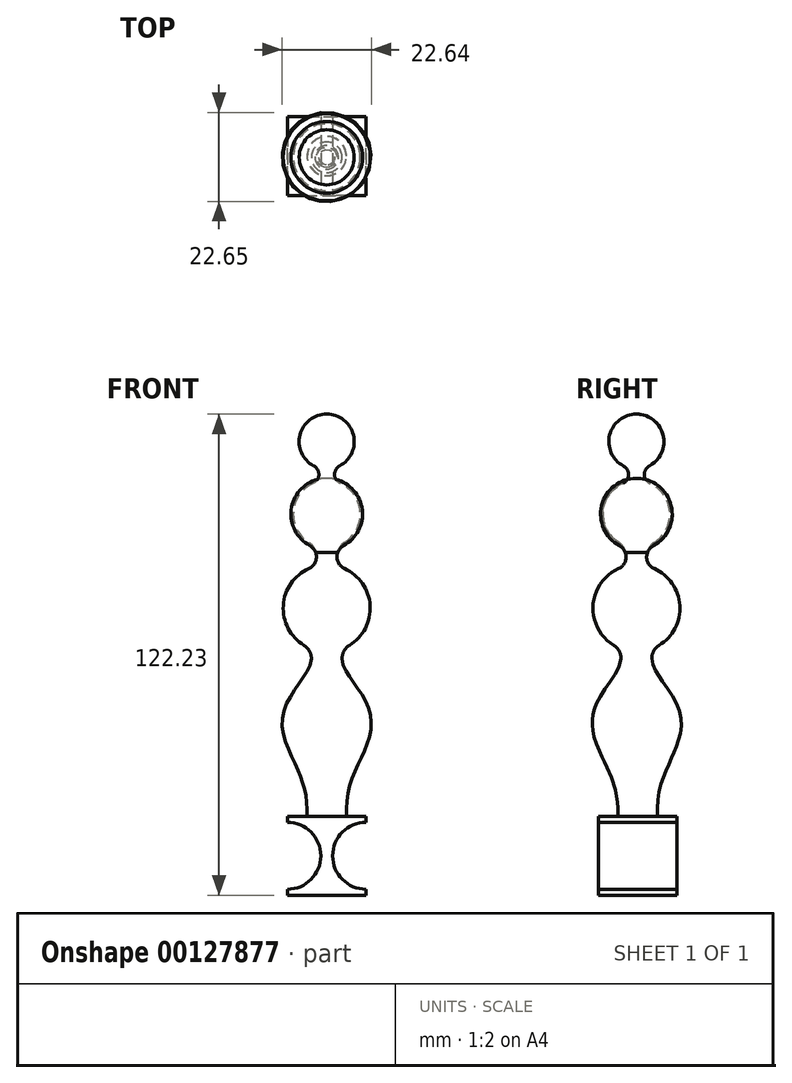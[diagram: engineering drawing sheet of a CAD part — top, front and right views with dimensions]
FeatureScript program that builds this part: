
annotation { "Feature Type Name" : "Feature", "Feature Type Description" : "" }
export const myFeature = defineFeature(function(context is Context, id is Id, definition is map)
    precondition{}
    {
        {
            var Q0;
            Q0=qCreatedBy(makeId("Top.planeOp"),FACE);
            var sketch = newSketch(context, id + "F0", { "sketchPlane" : qUnion([Q0])});
            skLineSegment(sketch, "E0.bottom", {"start": v(-10, -10) * mm, "end": v(10, -10) * mm});
            skLineSegment(sketch, "E0.top", {"start": v(-10, 10) * mm, "end": v(10, 10) * mm});
            skLineSegment(sketch, "E0.left", {"start": v(-10, -10) * mm, "end": v(-10, 10) * mm});
            skLineSegment(sketch, "E0.right", {"start": v(10, -10) * mm, "end": v(10, 10) * mm});
            skPoint(sketch, "E0.middle", {"position": v(0, 0) * mm});
            skSolve(sketch);
        }
        {
            var Q0;
            Q0=makeQuery(id+"F0.imprint","IMPRINT",FACE,{"disambiguationData":[TD([[makeQuery(id+"F0.imprint","IMPRINT",EDGE,{"derivedFrom":sQuery(id+"F0.wireOp",EDGE,"E0.bottom")}),1.0]])]});
            extrude(context, id + "F1", {"entities" : qUnion([Q0]), "depth" : 20 * mm});
        }
        {
            var Q0;
            Q0=makeQuery(id+"F1.opExtrude","SWEPT_FACE",FACE,{"disambiguationData":[OSD([sQuery(id+"F0.wireOp",EDGE,"E0.bottom")])]});
            var sketch = newSketch(context, id + "F2", { "sketchPlane" : qUnion([Q0])});
            skCircle(sketch, "E1", {"center": v(-10, 10) * mm, "radius": 8.5 * mm});
            skCircle(sketch, "E2", {"center": v(10, 10) * mm, "radius": 8.5 * mm});
            skSolve(sketch);
        }
        {
            var Q0;
            {var subQ0=sQuery(id+"F2.wireOp",EDGE,"E2");var subQ1=makeQuery(id+"F1.opExtrude","SWEPT_EDGE",EDGE,{"disambiguationData":[OSD([sQuery(id+"F0.wireOp",EDGE,"E0.bottom"),sQuery(id+"F0.wireOp",EDGE,"E0.right")])]});var subQ2=makeQuery(id+"F2.imprint","INTERSECT",VERTEX,{"disambiguationData":[OD(0.0)],"derivedFrom":[subQ1,subQ0]});Q0=makeQuery(id+"F2.imprint","IMPRINT",FACE,{"disambiguationData":[TD([[makeQuery(id+"F2.imprint","IMPRINT",EDGE,{"disambiguationData":[TD([[subQ2,1.0]])],"derivedFrom":subQ0}),1.0]])]});}
            var Q1;
            {var subQ0=sQuery(id+"F2.wireOp",EDGE,"E1");var subQ1=makeQuery(id+"F1.opExtrude","SWEPT_EDGE",EDGE,{"disambiguationData":[OSD([sQuery(id+"F0.wireOp",EDGE,"E0.bottom"),sQuery(id+"F0.wireOp",EDGE,"E0.left")])]});var subQ2=makeQuery(id+"F2.imprint","INTERSECT",VERTEX,{"disambiguationData":[OD(0.0)],"derivedFrom":[subQ1,subQ0]});Q1=makeQuery(id+"F2.imprint","IMPRINT",FACE,{"disambiguationData":[TD([[makeQuery(id+"F2.imprint","IMPRINT",EDGE,{"disambiguationData":[TD([[subQ2,-1.0]])],"derivedFrom":subQ0}),1.0]])]});}
            extrude(context, id + "F3", {"entities" : qUnion([Q0, Q1]), "operationType" : NewBodyOperationType.REMOVE, "endBound" : BoundingType.THROUGH_ALL, "oppositeDirection" : true, "depth" : 25 * mm});
        }
        {
            var Q0;
            Q0=qCreatedBy(makeId("Right.planeOp"),FACE);
            var sketch = newSketch(context, id + "F4", { "sketchPlane" : qUnion([Q0])});
            skLineSegment(sketch, "E3.0", {"start": v(-10, 20) * mm, "end": v(10, 20) * mm, "construction": true});
            skArc(sketch, "E4", {"start": v(0, 20) * mm, "mid": v(2.28, 37.3) * mm, "end": v(8.96, 53.42) * mm});
            skLineSegment(sketch, "E5", {"start": v(0, 20) * mm, "end": v(66.85, 20) * mm, "construction": true});
            skLineSegment(sketch, "E6", {"start": v(66.85, 20) * mm, "end": v(8.96, 53.42) * mm, "construction": true});
            skCircle(sketch, "E7", {"center": v(8.96, 53.42) * mm, "radius": 8.5 * mm});
            skLineSegment(sketch, "E8", {"start": v(8.96, 53.42) * mm, "end": v(27.36, 85.3) * mm, "construction": true});
            skCircle(sketch, "E9", {"center": v(18.16, 69.36) * mm, "radius": 7 * mm});
            skCircle(sketch, "E10", {"center": v(10.08, 64.37) * mm, "radius": 2.5 * mm});
            skPoint(sketch, "E11", {"position": v(1.49, 49.36) * mm});
            skPoint(sketch, "E12", {"position": v(13.2, 60.78) * mm});
            skPoint(sketch, "E13", {"position": v(12.2, 65.68) * mm});
            skPoint(sketch, "E14", {"position": v(9.82, 61.88) * mm});
            skPoint(sketch, "E15", {"position": v(21.66, 75.42) * mm});
            skLineSegment(sketch, "E16", {"start": v(21.66, 75.42) * mm, "end": v(0, 37.91) * mm});
            skCircle(sketch, "E17", {"center": v(-1.15, 47.93) * mm, "radius": 3 * mm});
            skLineSegment(sketch, "E18", {"start": v(4.05, 44.93) * mm, "end": v(1.45, 46.43) * mm});
            skLineSegment(sketch, "E19", {"start": v(1.45, 46.43) * mm, "end": v(-2.2, 48.54) * mm, "construction": true});
            skArc(sketch, "E20", {"start": v(0, 20) * mm, "mid": v(1.02, 32.63) * mm, "end": v(4.05, 44.93) * mm});
            skSolve(sketch);
        }
        {
            var Q0;
            {var subQ5=sQuery(id+"F4.wireOp",EDGE,"E18");Q0=makeQuery(id+"F4.imprint","IMPRINT",FACE,{"disambiguationData":[TD([[makeQuery(id+"F4.imprint","IMPRINT",EDGE,{"derivedFrom":subQ5}),-1.0]])]});}
            var Q1;
            {var subQ2=sQuery(id+"F4.wireOp",EDGE,"E7");var subQ4=makeQuery(id+"F4.imprint","INTERSECT",VERTEX,{"derivedFrom":[subQ2,sQuery(id+"F4.wireOp",EDGE,"E10")]});Q1=makeQuery(id+"F4.imprint","IMPRINT",FACE,{"disambiguationData":[TD([[makeQuery(id+"F4.imprint","IMPRINT",EDGE,{"disambiguationData":[TD([[subQ4,1.0]])],"derivedFrom":subQ2}),1.0]])]});}
            var Q2;
            {var subQ0=sQuery(id+"F4.wireOp",EDGE,"E10");var subQ1=sQuery(id+"F4.wireOp",EDGE,"E7");var subQ2=makeQuery(id+"F4.imprint","INTERSECT",VERTEX,{"derivedFrom":[subQ1,subQ0]});Q2=makeQuery(id+"F4.imprint","IMPRINT",FACE,{"disambiguationData":[TD([[makeQuery(id+"F4.imprint","IMPRINT",EDGE,{"disambiguationData":[TD([[subQ2,1.0]])],"derivedFrom":subQ1}),-1.0]])]});}
            var Q3;
            {var subQ0=sQuery(id+"F4.wireOp",EDGE,"E16");var subQ1=sQuery(id+"F4.wireOp",EDGE,"E9");var subQ2=makeQuery(id+"F4.imprint","INTERSECT",VERTEX,{"disambiguationData":[OD(0.0)],"derivedFrom":[subQ1,subQ0]});Q3=makeQuery(id+"F4.imprint","IMPRINT",FACE,{"disambiguationData":[TD([[makeQuery(id+"F4.imprint","IMPRINT",EDGE,{"disambiguationData":[TD([[subQ2,-1.0]])],"derivedFrom":subQ1}),1.0]])]});}
            var Q4;
            Q4=sQuery(id+"F4.wireOp",EDGE,"E16");
            revolve(context, id + "F5", {"entities" : qUnion([Q0, Q1, Q2, Q3]), "axis" : qUnion([Q4]), "revolveType" : RevolveType.FULL});
        }
        {
            var Q0;
            Q0=makeQuery(id+"F1.opExtrude","CAP_FACE",FACE,{"disambiguationData":[OSD([sQuery(id+"F0.wireOp",EDGE,"E0.bottom"),sQuery(id+"F0.wireOp",EDGE,"E0.top"),sQuery(id+"F0.wireOp",EDGE,"E0.left"),sQuery(id+"F0.wireOp",EDGE,"E0.right")])],"isStart":false});
            var sketch = newSketch(context, id + "F6", { "sketchPlane" : qUnion([Q0])});
            skCircle(sketch, "E21", {"center": v(0, 0) * mm, "radius": 5 * mm});
            skSolve(sketch);
        }
        {
            var Q0;
            Q0=qCreatedBy(makeId("Right.planeOp"),FACE);
            var sketch = newSketch(context, id + "F7", { "sketchPlane" : qUnion([Q0])});
            skPoint(sketch, "E22.0", {"position": v(8.96, 53.42) * mm});
            skPoint(sketch, "E23.0", {"position": v(18.16, 69.36) * mm});
            skLineSegment(sketch, "E24", {"start": v(8.96, 53.42) * mm, "end": v(18.16, 69.36) * mm, "construction": true});
            skSolve(sketch);
        }
        {
            var Q0;
            Q0=makeQuery(id+"F5.opRevolve","SWEPT_BODY",BODY,{"disambiguationData":[OSD([sQuery(id+"F4.wireOp",EDGE,"E7"),sQuery(id+"F4.wireOp",EDGE,"E9"),sQuery(id+"F4.wireOp",EDGE,"E10"),sQuery(id+"F4.wireOp",EDGE,"E16"),sQuery(id+"F4.wireOp",EDGE,"E17"),sQuery(id+"F4.wireOp",EDGE,"E18")])]});
            var Q1;
            Q1=sQuery(id+"F7.wireOp",EDGE,"E24");
            transform(context, id + "F8", {"entities" : qUnion([Q0]), "transformType" : TransformType.TRANSLATION_ENTITY, "oppositeDirectionEntity" : false, "transformLine" : qUnion([Q1]), "makeCopy" : true});
        }
        {
            var Q0;
            Q0=makeQuery(id+"F5.opRevolve","SWEPT_BODY",BODY,{"disambiguationData":[OSD([sQuery(id+"F4.wireOp",EDGE,"E7"),sQuery(id+"F4.wireOp",EDGE,"E9"),sQuery(id+"F4.wireOp",EDGE,"E10"),sQuery(id+"F4.wireOp",EDGE,"E16"),sQuery(id+"F4.wireOp",EDGE,"E17"),sQuery(id+"F4.wireOp",EDGE,"E18")])]});
            var Q1;
            Q1=sQuery(id+"F7.wireOp",VERTEX,"E23.0");
            transform(context, id + "F9", {"entities" : qUnion([Q0]), "transformType" : TransformType.SCALE_UNIFORMLY, "scale" : 1.3, "scalePoint" : qUnion([Q1]), "makeCopy" : false});
        }
        {
            var Q0;
            Q0=makeQuery(id+"F5.opRevolve","SWEPT_BODY",BODY,{"disambiguationData":[OSD([sQuery(id+"F4.wireOp",EDGE,"E7"),sQuery(id+"F4.wireOp",EDGE,"E9"),sQuery(id+"F4.wireOp",EDGE,"E10"),sQuery(id+"F4.wireOp",EDGE,"E16"),sQuery(id+"F4.wireOp",EDGE,"E17"),sQuery(id+"F4.wireOp",EDGE,"E18")])]});
            var Q1;
            Q1=makeQuery(id+"F8.opPattern","COPY",BODY,{"derivedFrom":makeQuery(id+"F5.opRevolve","SWEPT_BODY",BODY,{"disambiguationData":[OSD([sQuery(id+"F4.wireOp",EDGE,"E7"),sQuery(id+"F4.wireOp",EDGE,"E9"),sQuery(id+"F4.wireOp",EDGE,"E10"),sQuery(id+"F4.wireOp",EDGE,"E16"),sQuery(id+"F4.wireOp",EDGE,"E17"),sQuery(id+"F4.wireOp",EDGE,"E18")])]}),"instanceName":"1"});
            var Q2;
            Q2=makeQuery(id+"F1.opExtrude","CAP_EDGE",EDGE,{"disambiguationData":[OSD([sQuery(id+"F0.wireOp",EDGE,"E0.bottom")])],"isStart":false});
            transform(context, id + "F10", {"entities" : qUnion([Q0, Q1]), "transformType" : TransformType.ROTATION, "transformAxis" : qUnion([Q2]), "angle" : 30 * degree, "makeCopy" : false});
        }
        {
            var Q0;
            Q0=makeQuery(id+"F5.opRevolve","SWEPT_BODY",BODY,{"disambiguationData":[OSD([sQuery(id+"F4.wireOp",EDGE,"E7"),sQuery(id+"F4.wireOp",EDGE,"E9"),sQuery(id+"F4.wireOp",EDGE,"E10"),sQuery(id+"F4.wireOp",EDGE,"E16"),sQuery(id+"F4.wireOp",EDGE,"E17"),sQuery(id+"F4.wireOp",EDGE,"E18")])]});
            var Q1;
            Q1=makeQuery(id+"F8.opPattern","COPY",BODY,{"derivedFrom":makeQuery(id+"F5.opRevolve","SWEPT_BODY",BODY,{"disambiguationData":[OSD([sQuery(id+"F4.wireOp",EDGE,"E7"),sQuery(id+"F4.wireOp",EDGE,"E9"),sQuery(id+"F4.wireOp",EDGE,"E10"),sQuery(id+"F4.wireOp",EDGE,"E16"),sQuery(id+"F4.wireOp",EDGE,"E17"),sQuery(id+"F4.wireOp",EDGE,"E18")])]}),"instanceName":"1"});
            transform(context, id + "F11", {"entities" : qUnion([Q0, Q1]), "transformType" : TransformType.TRANSLATION_3D, "dx" : 0 * mm, "dy" : 10 * mm, "dz" : 20 * mm, "makeCopy" : false});
        }
        {
            var Q1;
            Q1=makeQuery(id+"F6.imprint","IMPRINT",FACE,{"disambiguationData":[TD([[makeQuery(id+"F6.imprint","IMPRINT",EDGE,{"derivedFrom":sQuery(id+"F6.wireOp",EDGE,"E21")}),1.0]])]});
            var Q2;
            Q2=makeQuery(id+"F5.opRevolve","SWEPT_FACE",FACE,{"disambiguationData":[OSD([sQuery(id+"F4.wireOp",EDGE,"E18")])]});
            var Q3;
            Q3=sQuery(id+"F4.wireOp",EDGE,"E20");
            loft(context, id + "F12", {"operationType" : NewBodyOperationType.ADD, "startCondition" : LoftEndDerivativeType.NORMAL_TO_PROFILE, "startMagnitude" : 1, "endCondition" : LoftEndDerivativeType.MATCH_CURVATURE, "endMagnitude" : 1, "sheetProfilesArray" : [{ "sheetProfileEntities" : qUnion([Q1]) }, { "sheetProfileEntities" : qUnion([Q2]) }], "guidesArray" : [{ "guideEntities" : qUnion([Q3]), "guideDerivativeType" : LoftGuideDerivativeType.DEFAULT, "guideDerivativeMagnitude" : 1 }]});
        }
    });
